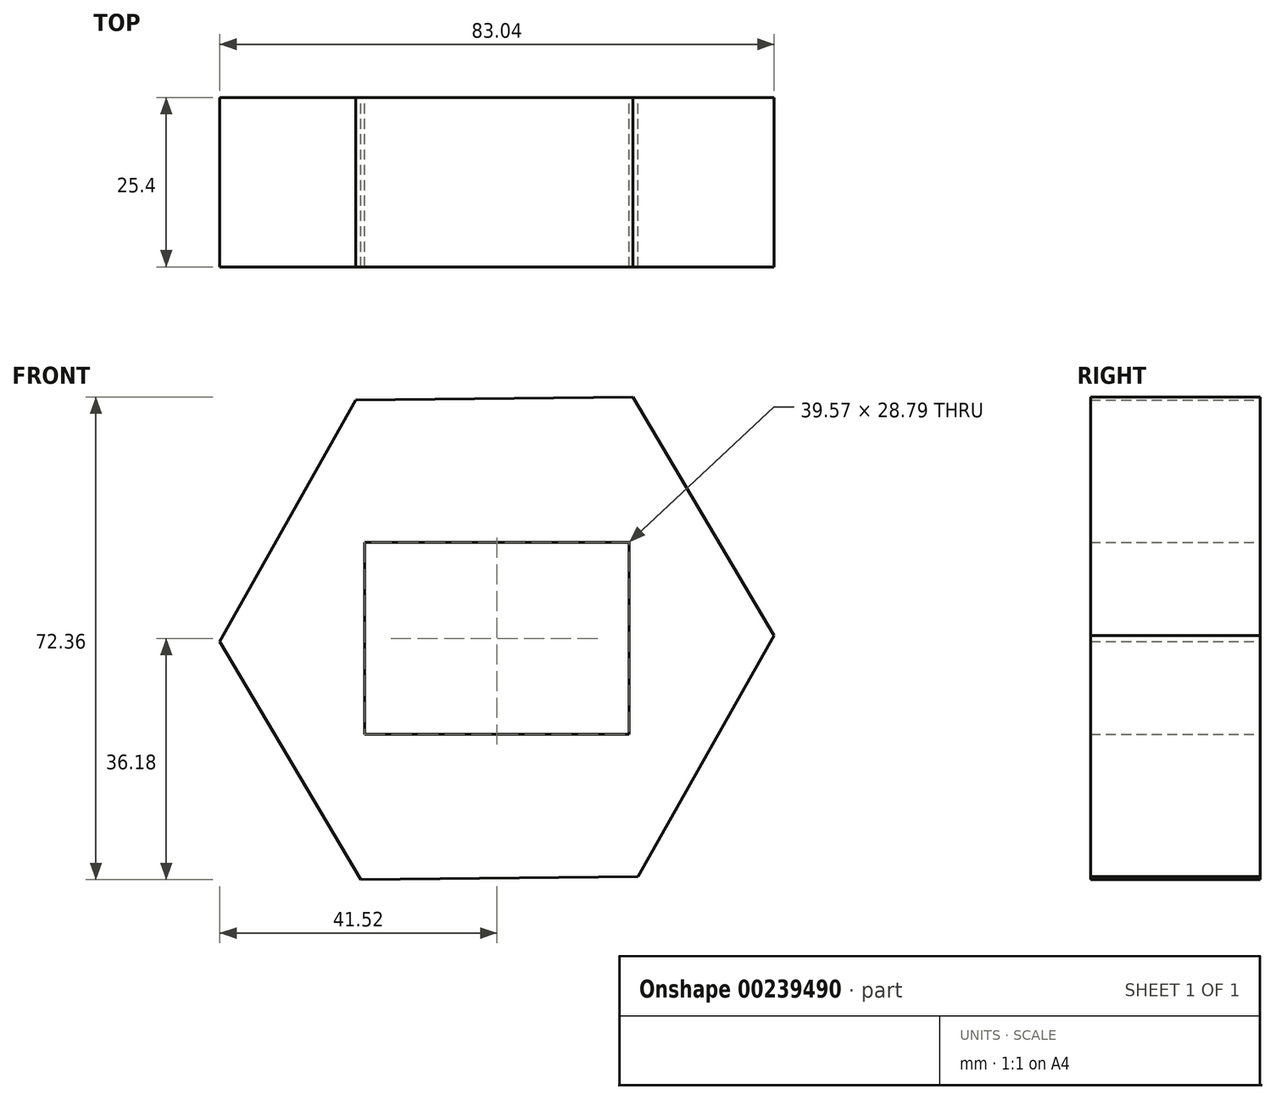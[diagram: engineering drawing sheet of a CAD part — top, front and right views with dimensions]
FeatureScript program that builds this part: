
annotation { "Feature Type Name" : "Feature", "Feature Type Description" : "" }
export const myFeature = defineFeature(function(context is Context, id is Id, definition is map)
    precondition{}
    {
        {
            var Q0;
            Q0=qCreatedBy(makeId("Front.planeOp"),FACE);
            var sketch = newSketch(context, id + "F0", { "sketchPlane" : qUnion([Q0])});
            skCircle(sketch, "E0.cCircle", {"center": v(0, 0) * mm, "radius": 35.96 * mm, "construction": true});
            skLineSegment(sketch, "E0.0", {"start": v(20.37, 36.18) * mm, "end": v(41.52, 0.45) * mm});
            skLineSegment(sketch, "E0.1", {"start": v(41.52, 0.45) * mm, "end": v(21.15, -35.73) * mm});
            skLineSegment(sketch, "E0.2", {"start": v(21.15, -35.73) * mm, "end": v(-20.37, -36.18) * mm});
            skLineSegment(sketch, "E0.3", {"start": v(-20.37, -36.18) * mm, "end": v(-41.52, -0.45) * mm});
            skLineSegment(sketch, "E0.4", {"start": v(-41.52, -0.45) * mm, "end": v(-21.15, 35.73) * mm});
            skLineSegment(sketch, "E0.5", {"start": v(-21.15, 35.73) * mm, "end": v(20.37, 36.18) * mm});
            skPoint(sketch, "E0.0.midPoint", {"position": v(30.95, 18.31) * mm});
            skSolve(sketch);
        }
        {
            var Q0;
            Q0 = qSketchRegion(id + "F0", true);
            extrude(context, id + "F1", {"entities" : qUnion([Q0]), "depth" : 25.4 * mm});
        }
        {
            var Q0;
            Q0=qCreatedBy(makeId("Front.planeOp"),FACE);
            var sketch = newSketch(context, id + "F2", { "sketchPlane" : qUnion([Q0])});
            skLineSegment(sketch, "E1.bottom", {"start": v(19.79, 14.4) * mm, "end": v(-19.79, 14.4) * mm});
            skLineSegment(sketch, "E1.top", {"start": v(19.79, -14.4) * mm, "end": v(-19.79, -14.4) * mm});
            skLineSegment(sketch, "E1.left", {"start": v(19.79, 14.4) * mm, "end": v(19.79, -14.4) * mm});
            skLineSegment(sketch, "E1.right", {"start": v(-19.79, 14.4) * mm, "end": v(-19.79, -14.4) * mm});
            skPoint(sketch, "E1.middle", {"position": v(0, 0) * mm});
            skSolve(sketch);
        }
        {
            var Q0;
            Q0 = qSketchRegion(id + "F2", true);
            extrude(context, id + "F3", {"entities" : qUnion([Q0]), "operationType" : NewBodyOperationType.REMOVE, "depth" : 121.4 * mm});
        }
    });
